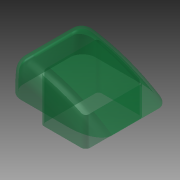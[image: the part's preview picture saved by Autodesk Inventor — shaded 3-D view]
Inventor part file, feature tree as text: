
AUTODESK INVENTOR PART (.ipt)
format: ipt  version: 2015 (Build 190159000, 159)  size: 297,472 bytes
history: native  units: in
note: dims shown in document units (in); Inventor stores cm internally (conversion verified against a paired STEP export)
features: extrude x3, sketch x3, fillet x2, shell x2
ambient origin geometry x8: Origin, YZ Plane, XZ Plane, XY Plane, X Axis, Y Axis, Z Axis, Center Point
bodies: Solid1 (feature_tree)
feature tree (10):
  extrude  "Extrusion1"  Depth=6.0in
  fillet  "Fillet1"  Radius=6.0in
  fillet  "Fillet2"  Radius=0.4in
  shell  "Shell1"  Thickness=0.64in
  extrude  "Extrusion2"  Depth=6.0in TaperAngle=0.0deg
  extrude  "Extrusion3"  Depth=0.15in
  shell  "Shell2"  Thickness=0.07in
  sketch  "Sketch1"  dims[d0=3.04in d4=3.01in d7=6.0in d8=0.4in d9=0.64in]
  sketch  "Sketch2"  dims[d10=6.0in d11=2.55in d12=0.0in]
  sketch  "Sketch3"  dims[d13=0.5in d14=0.5in d15=0.07in d16=0.68in d17=2.22in d18=2.26in d19=0.29in d20=0.15in d21=1.455in d22=0.0in d23=0.15in d24=0.29in d25=2.26in d26=2.22in d27=0.67in d28=0.0in d29=0.05in]
